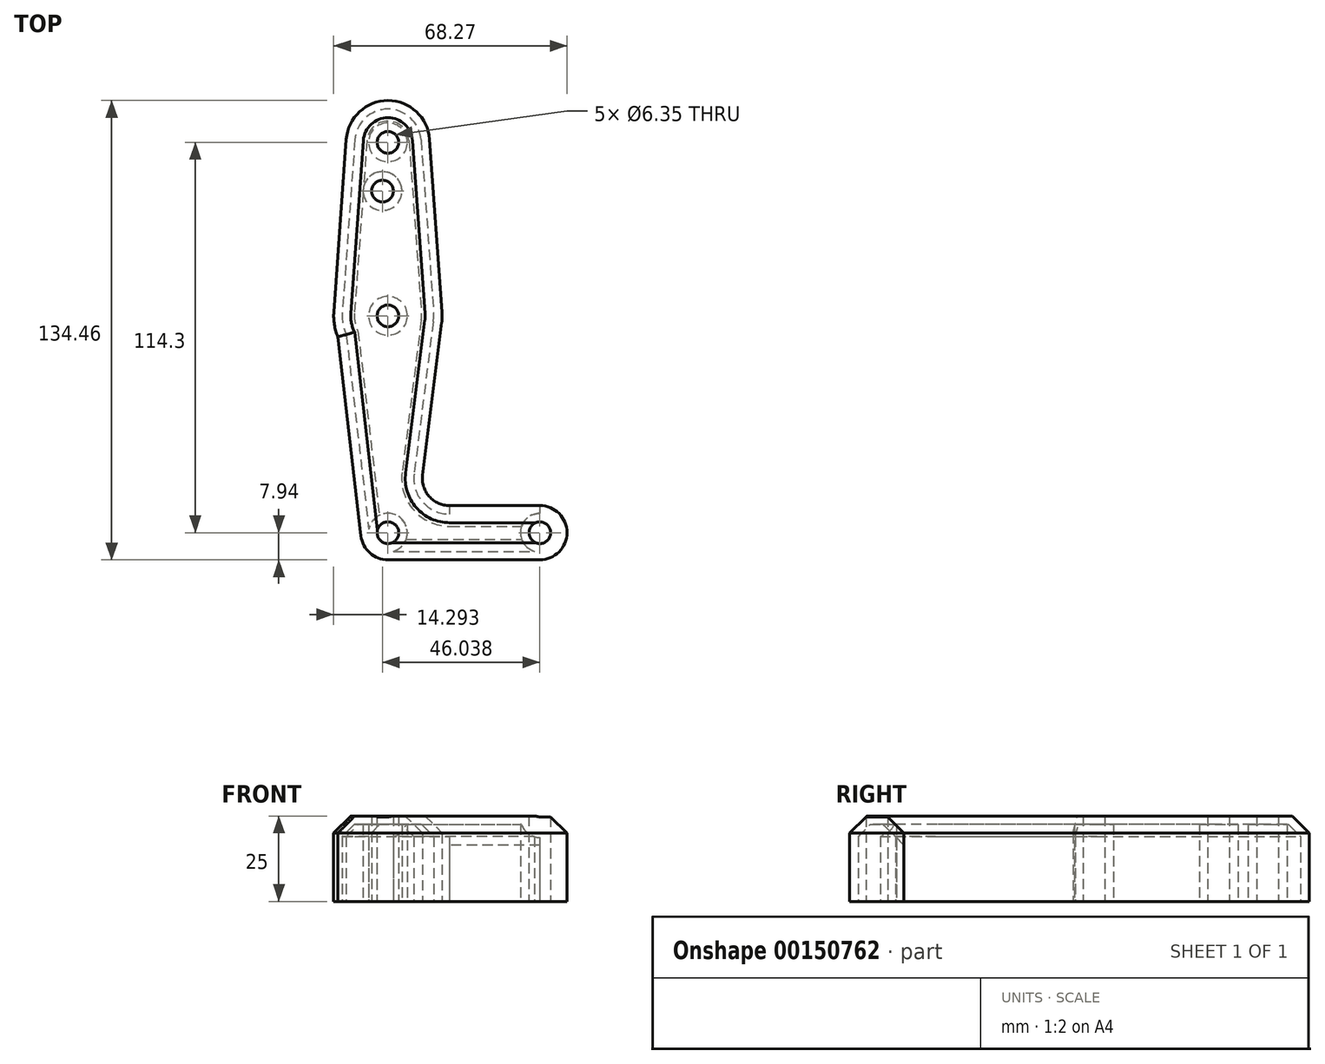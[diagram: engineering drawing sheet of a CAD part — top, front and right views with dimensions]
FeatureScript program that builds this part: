
annotation { "Feature Type Name" : "Feature", "Feature Type Description" : "" }
export const myFeature = defineFeature(function(context is Context, id is Id, definition is map)
    precondition{}
    {
        {
            var Q0;
            Q0=qCreatedBy(makeId("Top.planeOp"),FACE);
            var sketch = newSketch(context, id + "F0", { "sketchPlane" : qUnion([Q0])});
            skCircle(sketch, "E0", {"center": v(0, 50.8) * mm, "radius": 12.22 * mm});
            skCircle(sketch, "E1", {"center": v(0, 0) * mm, "radius": 15.88 * mm});
            skCircle(sketch, "E2", {"center": v(0, -63.5) * mm, "radius": 7.94 * mm});
            skCircle(sketch, "E3", {"center": v(44.45, -63.5) * mm, "radius": 7.94 * mm});
            skLineSegment(sketch, "E4", {"start": v(-12.19, 51.68) * mm, "end": v(-15.92, 0) * mm});
            skLineSegment(sketch, "E5", {"start": v(12.19, 51.68) * mm, "end": v(15.83, 1.14) * mm});
            skLineSegment(sketch, "E6", {"start": v(-14.64, -6.13) * mm, "end": v(-7.88, -64.41) * mm});
            skLineSegment(sketch, "E7", {"start": v(0, -55.56) * mm, "end": v(0, -55.56) * mm});
            skLineSegment(sketch, "E8", {"start": v(0, -71.44) * mm, "end": v(44.45, -71.44) * mm});
            skLineSegment(sketch, "E9", {"start": v(15.75, -1.98) * mm, "end": v(10.13, -46.62) * mm});
            skLineSegment(sketch, "E10.trimOffspring", {"start": v(18.01, -55.56) * mm, "end": v(44.45, -55.56) * mm});
            skPoint(sketch, "E11.visualSharp", {"position": v(9, -55.56) * mm});
            skArc(sketch, "E11.filletArc", {"start": v(10.13, -46.62) * mm, "mid": v(12.05, -52.87) * mm, "end": v(18.01, -55.56) * mm});
            skCircle(sketch, "E12", {"center": v(0, 50.8) * mm, "radius": 3.18 * mm});
            skCircle(sketch, "E13", {"center": v(0, 0) * mm, "radius": 3.17 * mm});
            skCircle(sketch, "E14", {"center": v(-1.59, 36.53) * mm, "radius": 3.18 * mm});
            skCircle(sketch, "E15", {"center": v(0, -63.5) * mm, "radius": 3.18 * mm});
            skCircle(sketch, "E16", {"center": v(44.45, -63.5) * mm, "radius": 3.18 * mm});
            skLineSegment(sketch, "E17", {"start": v(0, 71.86) * mm, "end": v(0, -75.51) * mm, "construction": true});
            skSolve(sketch);
        }
        {
            var Q0;
            {var subQ0=sQuery(id+"F0.wireOp",EDGE,"E6");Q0=makeQuery(id+"F0.imprint","IMPRINT",FACE,{"disambiguationData":[TD([[makeQuery(id+"F0.imprint","IMPRINT",EDGE,{"derivedFrom":subQ0}),1.0]])]});}
            var Q1;
            Q1=makeQuery(id+"F0.imprint","IMPRINT",FACE,{"disambiguationData":[TD([[makeQuery(id+"F0.imprint","IMPRINT",EDGE,{"derivedFrom":sQuery(id+"F0.wireOp",EDGE,"E16")}),-1.0]])]});
            var Q2;
            Q2=makeQuery(id+"F0.imprint","IMPRINT",FACE,{"disambiguationData":[TD([[makeQuery(id+"F0.imprint","IMPRINT",EDGE,{"derivedFrom":sQuery(id+"F0.wireOp",EDGE,"E15")}),-1.0]])]});
            var Q3;
            {var subQ5=sQuery(id+"F0.wireOp",EDGE,"E5");Q3=makeQuery(id+"F0.imprint","IMPRINT",FACE,{"disambiguationData":[TD([[makeQuery(id+"F0.imprint","IMPRINT",EDGE,{"derivedFrom":subQ5}),-1.0]])]});}
            var Q4;
            Q4=makeQuery(id+"F0.imprint","IMPRINT",FACE,{"disambiguationData":[TD([[makeQuery(id+"F0.imprint","IMPRINT",EDGE,{"derivedFrom":sQuery(id+"F0.wireOp",EDGE,"E12")}),-1.0]])]});
            var Q5;
            Q5=makeQuery(id+"F0.imprint","IMPRINT",FACE,{"disambiguationData":[TD([[makeQuery(id+"F0.imprint","IMPRINT",EDGE,{"derivedFrom":sQuery(id+"F0.wireOp",EDGE,"E13")}),-1.0]])]});
            extrude(context, id + "F1", {"entities" : qUnion([Q0, Q1, Q2, Q3, Q4, Q5]), "depth" : 25 * mm});
        }
        {
            var Q0;
            Q0=makeQuery(id+"F1.opExtrude","CAP_EDGE",EDGE,{"disambiguationData":[OSD([sQuery(id+"F0.wireOp",EDGE,"E9")])],"isStart":false});
            var Q1;
            {var subQ0=sQuery(id+"F0.wireOp",EDGE,"E1");Q1=makeQuery(id+"F1.opExtrude","CAP_EDGE",EDGE,{"disambiguationData":[OSD([subQ0]),TDD([makeQuery(id+"F0.imprint","IMPRINT",EDGE,{"disambiguationData":[TD([[makeQuery(id+"F0.imprint","INTERSECT",VERTEX,{"derivedFrom":[subQ0,sQuery(id+"F0.wireOp",EDGE,"E5")]}),1.0]])],"derivedFrom":subQ0})])],"isStart":false});}
            var Q2;
            Q2=makeQuery(id+"F1.opExtrude","CAP_EDGE",EDGE,{"disambiguationData":[OSD([sQuery(id+"F0.wireOp",EDGE,"E5")])],"isStart":false});
            chamfer(context, id + "F2", {"entities" : qUnion([Q0, Q1, Q2]), "width" : 5 * mm, "tangentPropagation" : true});
        }
        {
            var Q0;
            Q0=makeQuery(id+"F1.opExtrude","CAP_FACE",FACE,{"disambiguationData":[OSD([sQuery(id+"F0.wireOp",EDGE,"E0"),sQuery(id+"F0.wireOp",EDGE,"E1"),sQuery(id+"F0.wireOp",EDGE,"E2"),sQuery(id+"F0.wireOp",EDGE,"E3"),sQuery(id+"F0.wireOp",EDGE,"E4"),sQuery(id+"F0.wireOp",EDGE,"E5"),sQuery(id+"F0.wireOp",EDGE,"E6"),sQuery(id+"F0.wireOp",EDGE,"E8"),sQuery(id+"F0.wireOp",EDGE,"E9"),sQuery(id+"F0.wireOp",EDGE,"E10.trimOffspring"),sQuery(id+"F0.wireOp",EDGE,"E11.filletArc"),sQuery(id+"F0.wireOp",EDGE,"E12"),sQuery(id+"F0.wireOp",EDGE,"E13"),sQuery(id+"F0.wireOp",EDGE,"E14"),sQuery(id+"F0.wireOp",EDGE,"E15"),sQuery(id+"F0.wireOp",EDGE,"E16")])],"isStart":true});
            var Q1;
            Q1=makeQuery(id+"F1.opExtrude","SWEPT_FACE",FACE,{"disambiguationData":[OSD([sQuery(id+"F0.wireOp",EDGE,"E10.trimOffspring")])]});
            shell(context, id + "F3", {"entities" : qUnion([Q0, Q1]), "thickness" : 2.5 * mm});
        }
    });
